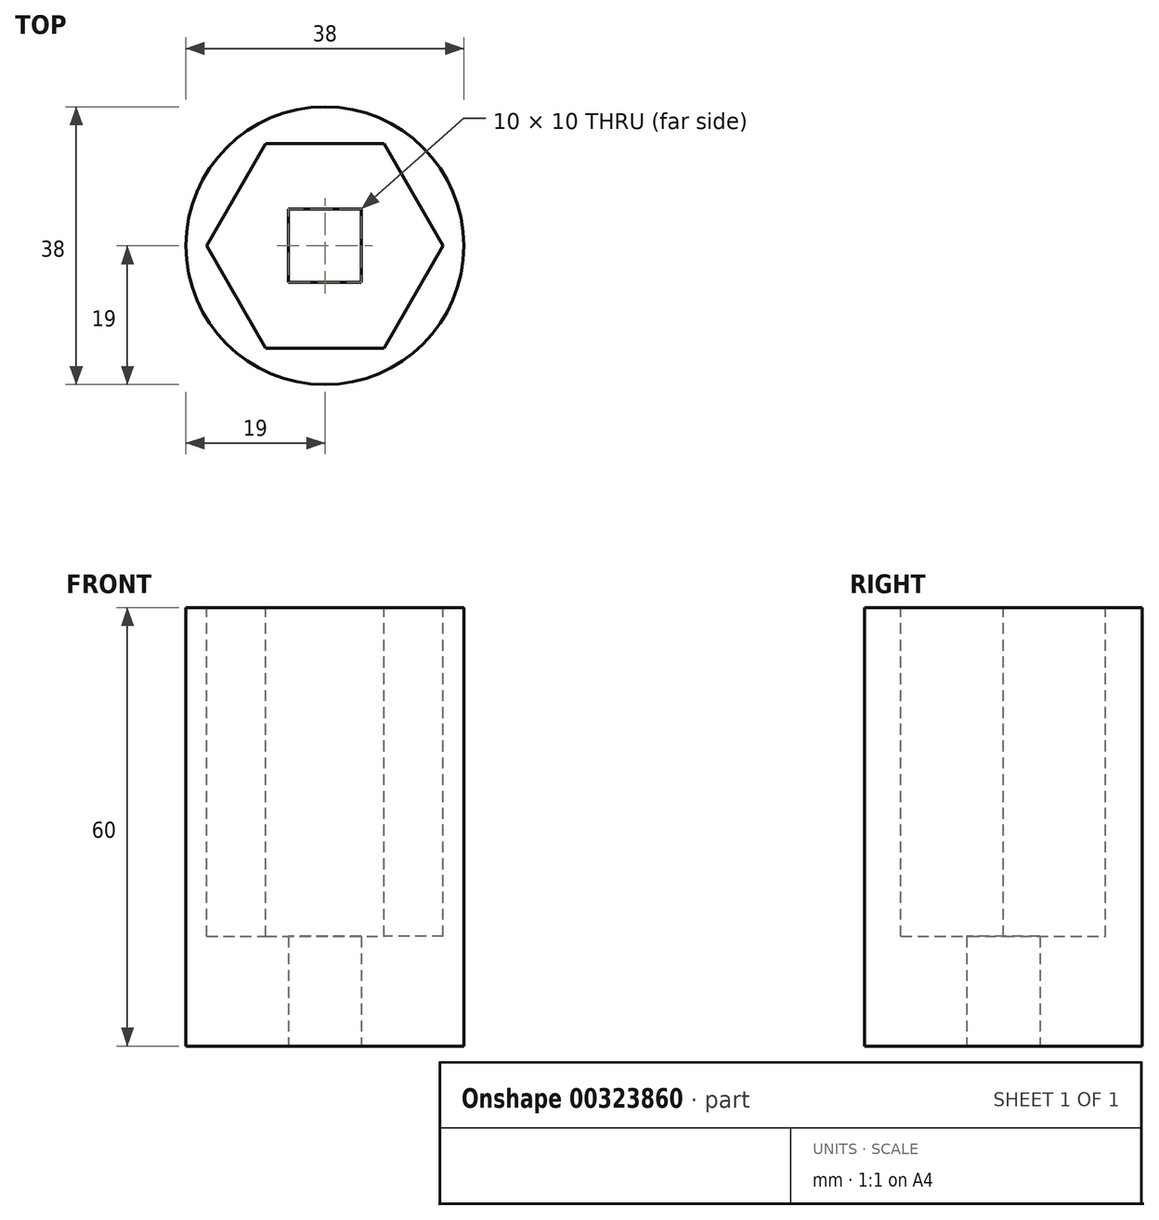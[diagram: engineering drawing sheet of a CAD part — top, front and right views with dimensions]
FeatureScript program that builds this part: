
annotation { "Feature Type Name" : "Feature", "Feature Type Description" : "" }
export const myFeature = defineFeature(function(context is Context, id is Id, definition is map)
    precondition{}
    {
        {
            var Q0;
            Q0=qCreatedBy(makeId("Top.planeOp"),FACE);
            var sketch = newSketch(context, id + "F0", { "sketchPlane" : qUnion([Q0])});
            skCircle(sketch, "E0", {"center": v(0, 0) * mm, "radius": 19 * mm});
            skSolve(sketch);
        }
        {
            var Q0;
            Q0=makeQuery(id+"F0.imprint","IMPRINT",FACE,{"disambiguationData":[TD([[makeQuery(id+"F0.imprint","IMPRINT",EDGE,{"derivedFrom":sQuery(id+"F0.wireOp",EDGE,"E0")}),1.0]])]});
            extrude(context, id + "F1", {"entities" : qUnion([Q0]), "depth" : 60 * mm});
        }
        {
            var Q0;
            Q0=makeQuery(id+"F1.opExtrude","CAP_FACE",FACE,{"disambiguationData":[OSD([sQuery(id+"F0.wireOp",EDGE,"E0")])],"isStart":false});
            var sketch = newSketch(context, id + "F2", { "sketchPlane" : qUnion([Q0])});
            skCircle(sketch, "E1.cCircle", {"center": v(0, 0) * mm, "radius": 14 * mm, "construction": true});
            skLineSegment(sketch, "E1.0", {"start": v(-8.08, 14) * mm, "end": v(8.08, 14) * mm});
            skLineSegment(sketch, "E1.1", {"start": v(8.08, 14) * mm, "end": v(16.17, 0) * mm});
            skLineSegment(sketch, "E1.2", {"start": v(16.17, 0) * mm, "end": v(8.08, -14) * mm});
            skLineSegment(sketch, "E1.3", {"start": v(8.08, -14) * mm, "end": v(-8.08, -14) * mm});
            skLineSegment(sketch, "E1.4", {"start": v(-8.08, -14) * mm, "end": v(-16.17, 0) * mm});
            skLineSegment(sketch, "E1.5", {"start": v(-16.17, 0) * mm, "end": v(-8.08, 14) * mm});
            skPoint(sketch, "E1.0.midPoint", {"position": v(0, 14) * mm});
            skSolve(sketch);
        }
        {
            var Q0;
            Q0=makeQuery(id+"F2.imprint","IMPRINT",FACE,{"disambiguationData":[TD([[makeQuery(id+"F2.imprint","IMPRINT",EDGE,{"derivedFrom":sQuery(id+"F2.wireOp",EDGE,"E1.0")}),-1.0]])]});
            extrude(context, id + "F3", {"entities" : qUnion([Q0]), "operationType" : NewBodyOperationType.REMOVE, "oppositeDirection" : true, "depth" : 45 * mm});
        }
        {
            var Q0;
            Q0=makeQuery(id+"F1.opExtrude","CAP_FACE",FACE,{"disambiguationData":[OSD([sQuery(id+"F0.wireOp",EDGE,"E0")])],"isStart":true});
            var sketch = newSketch(context, id + "F4", { "sketchPlane" : qUnion([Q0])});
            skCircle(sketch, "E2.cCircle", {"center": v(0, 0) * mm, "radius": 5 * mm, "construction": true});
            skLineSegment(sketch, "E2.0", {"start": v(-5, 5) * mm, "end": v(5, 5) * mm});
            skLineSegment(sketch, "E2.1", {"start": v(5, 5) * mm, "end": v(5, -5) * mm});
            skLineSegment(sketch, "E2.2", {"start": v(5, -5) * mm, "end": v(-5, -5) * mm});
            skLineSegment(sketch, "E2.3", {"start": v(-5, -5) * mm, "end": v(-5, 5) * mm});
            skPoint(sketch, "E2.0.midPoint", {"position": v(0, 5) * mm});
            skSolve(sketch);
        }
        {
            var Q0;
            Q0=makeQuery(id+"F4.imprint","IMPRINT",FACE,{"disambiguationData":[TD([[makeQuery(id+"F4.imprint","IMPRINT",EDGE,{"derivedFrom":sQuery(id+"F4.wireOp",EDGE,"E2.0")}),-1.0]])]});
            extrude(context, id + "F5", {"entities" : qUnion([Q0]), "operationType" : NewBodyOperationType.REMOVE, "endBound" : BoundingType.UP_TO_NEXT, "oppositeDirection" : true, "depth" : 25 * mm});
        }
    });
